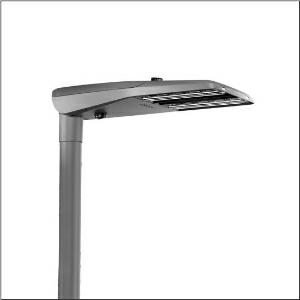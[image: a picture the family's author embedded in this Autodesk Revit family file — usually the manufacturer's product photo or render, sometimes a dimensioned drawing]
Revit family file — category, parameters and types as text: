
# Revit family: streetlight_sl_11_iq_midi___st1_2a_5xc3a51y08le_7352
name_source: partatom
category: Lighting Fixtures
units: mm (PartAtom-declared; Revit-internal decimal feet)

## family parameters
Cut with Voids When Loaded = No
Host = Face
Light Source = No
Part Type = Normal
Room Calculation Point = No
Round Connector Dimension = Use Diameter
Shared = No

## types (1)
- --- (1 x LED, 9210 lm, 59.4 W, 3000K)
    Apparent Load = 59 VA
    CIE Flux Codes = 32 70 96 100 100
    Color Rendering = 70
    Color Temperature = 3000K
    Default Elevation = 1800 mm
    Description = Streetlight SL 11 iQ midi, mast luminaire, primary light control with 3 zone facetted reflector, of plastic, silver coated, highly specular, primary optical cover: cover, of PMMA, transparent, light distribution: ST1.2a, light emission: direct distribution, primary light characteristic: asymmetric, installation type: post-top, side-entry, lamps: LED, High Power LED, rated values: 9.210lm | 59,4W | 155,1lm/W (begin service life); end service life: 9.210lm | 61,6W; at 50% lumin. flux: 4.605lm | 28,5W | 161,6lm/W, colour temperature: 3000K, colour rendering: CRI > 70, light colour: 730, light setting 1 begin service life: 100% | 9.210lm | 59,4W | 155,1lm/W | 3.000K, light setting 1 end service life: 61,6W, further light settings possible, control: pre-setting: logarithmic dimming characteristic, Street-Remote, Auto-Match, Temp-Guard, Lumen-Switch, Night-Set, Smart-Wire, Light-Fading, Desk-Remote (wireless, voltage-free reading and setting of iQ features in the workshop via application-optimized NFC function/RFID function), optimised constant luminous flux control (CLO 2.0), with cable H07RN-F 5x 1.5mm², mains connection: 230..240V, AC, 50/60Hz, connection cable pre-assembled, cable length: 8,5m, luminaire housing, of diecast aluminium, powder-coated, Siteco® metallic grey (DB 702S), please order mast flange separately, inclination adjustable without tools: 0°, 5°, 10°, 15° (post-top) | 0°, -5°, -10°, -15° (side-entry), sealing non-destructively replaceable, multi-level sealing system, length: 780mm, width: 376mm, height: 118mm, mast flange for spigot size: 42mm (side-entry): 5XC10008XM4, 60/48mm (side-entry/post-top): 5XC10108XM2, 76/60mm (side-entry/post-top): 5XC10108XM1, equipment: standard, Smart Interface below and above, protection rating (complete): IP66, insulation class (complete): insulation class II (safety insulation), certification: CE, ENEC, ENEC+, VDE, UKCA, impact resistance: IK10, permissible operating ambient temperature for outdoor applications: -25..+50°C, standard-compliant lighting for roads and squares, Environmental Product Declaration (EPD) tested and certified by an independent institute, packaging unit: 1 piece

Light Distribution: ST1.2a
    Height = 118 mm
    Lamp = 1 x LED
    Lamp Light Flux = 9210 lm
    Lamp Power = 59.4 W
    Lamp count = 1
    Length = 780 mm
    Luminous efficacy = 155 lm/W
    Manufacturer = Siteco
    ModVariant = No
    Model = 5XC3A51Y08LE
    Number of Poles = 1
    OnlyDefault = Yes
    Power Factor = 1
    Product Name = Streetlight SL 11 iQ midi | ST1.2a
    Product group = mast luminaire | pylon top
    ProductGroupID = 6100
    Protection Class = Protection class II
    Protection Degree = IP 66
    RLX_Detail_Level = 1
    RLX_Emergency_Light_Flux = 0 lm
    RLX_Emergency_Type = 0
    RLX_Emergency_Type_DB = No
    RlxData = <blob elided: 69797 chars, md5=5aa8df10>
    Socket = socket
    Standby Power = 0 W
    System Light Flux = 9210 lm
    System Power = 59 W
    Type Comments = factory setting: luminous flux: 100 % | dim-lin: 254 | 521 mA
    Type Image = l_1004429.jpg
    URL = http://relux.com
    VarID = @adj_133304
    Voltage = 0 V
    Weight = 0.00 kg
    Width = 376 mm

## geometry (parser evidence)
native form markers: Blend x4, Sweep x9
no freeform markers — native parametric forms only
